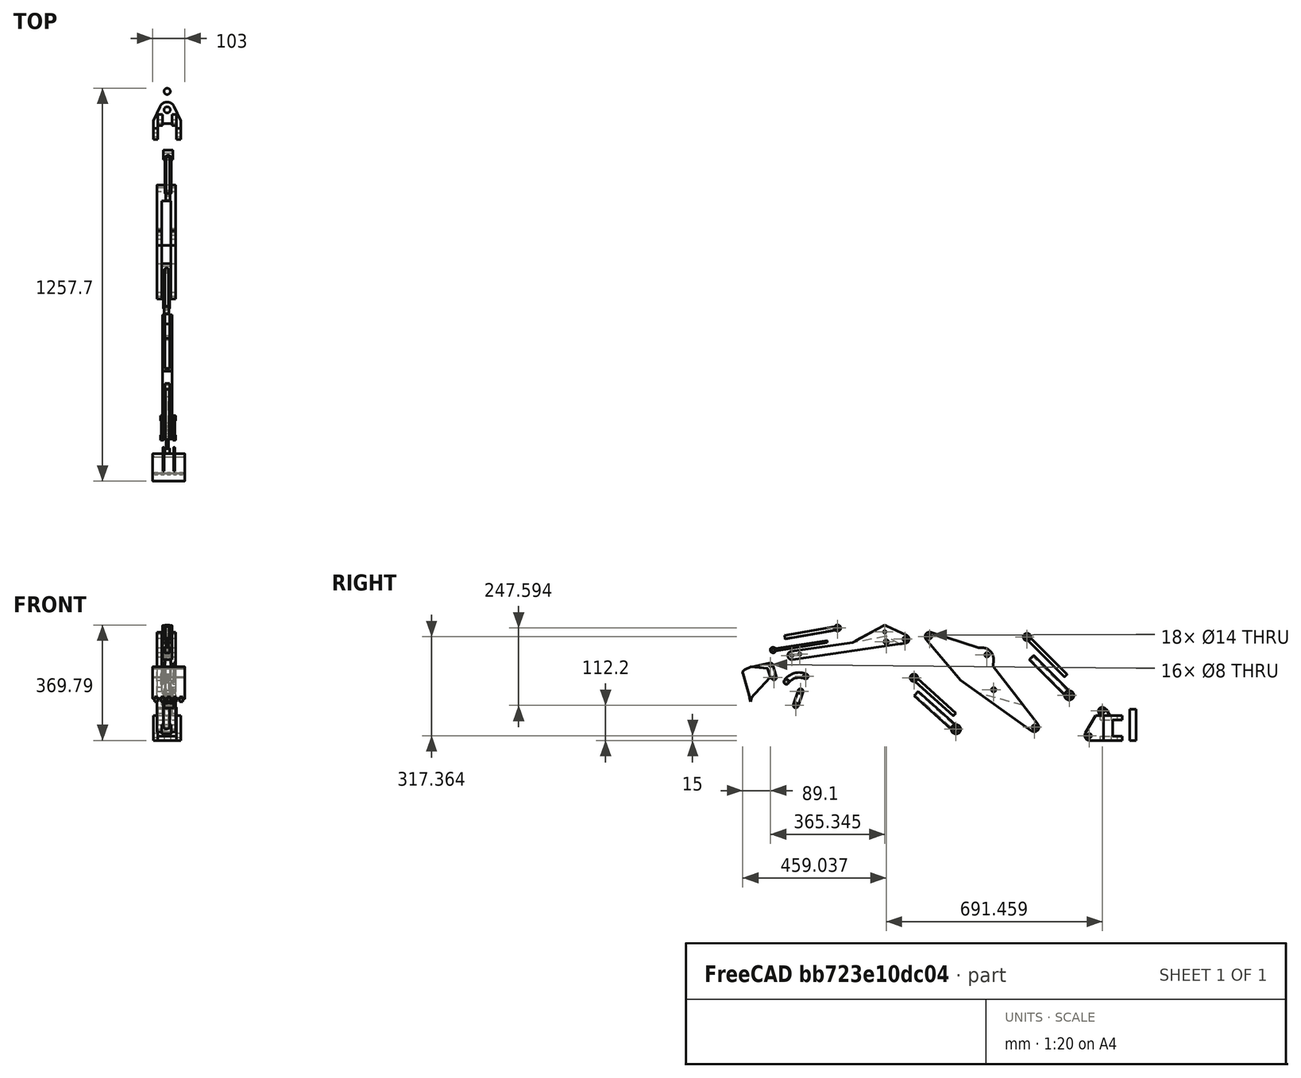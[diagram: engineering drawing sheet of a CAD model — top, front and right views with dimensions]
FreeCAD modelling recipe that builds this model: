
FCSTD DOCUMENT  (FreeCAD 0.22R38008 (Git))
Label: AssemblyExample
License: CC-BY 4.0
LicenseURL: https://creativecommons.org/licenses/by/4.0/
objects: App::FeaturePython×17, Part::Feature×13, App::Link×13, App::DocumentObjectGroup×1, Assembly::JointGroup×1, Assembly::AssemblyObject×1
note: 13 computed .brp shape members not serialized (recipe doc carries the construction recipe); baked Part::Feature solids carry a one-line shape summary decoded from their .brp

FEATURE [Part::Feature] Shape001  label="Base"
  shape: bbox 88 x 119.5 x 106 mm, 44 faces (baked)
FEATURE [Part::Feature] Shape012  label="BasePin"
  shape: bbox 20 x 20 x 100 mm, 3 faces (baked)
FEATURE [Part::Feature] Shape013  label="Stick"
  shape: bbox 30 x 388.4 x 109.8 mm, 24 faces (baked)
FEATURE [Part::Feature] Shape014  label="BucketLink1"
  shape: bbox 30 x 31.36 x 61.47 mm, 22 faces (baked)
FEATURE [Part::Feature] Shape015  label="Bucket"
  shape: bbox 103 x 108.6 x 124 mm, 97 faces (baked)
FEATURE [Part::Feature] Shape016  label="BoomCylinderInner"
  shape: bbox 15 x 140.2 x 140.2 mm, 6 faces (baked)
FEATURE [Part::Feature] Shape017  label="StickCylinderInner"
  shape: bbox 15 x 146.3 x 133.8 mm, 6 faces (baked)
FEATURE [Part::Feature] Shape018  label="BucketCylinderInner"
  shape: bbox 15 x 182.7 x 39.88 mm, 6 faces (baked)
FEATURE [Part::Feature] Shape019  label="BucketLink2"
  shape: bbox 48 x 78 x 37.57 mm, 23 faces (baked)
FEATURE [Part::Feature] Shape020  label="BoomCylinderOuter"
  shape: bbox 30 x 143 x 143 mm, 8 faces (baked)
FEATURE [Part::Feature] Shape021  label="StickCylinderOuter"
  shape: bbox 30 x 148.8 x 136.9 mm, 8 faces (baked)
FEATURE [Part::Feature] Shape022  label="BucketCylinderOuter"
  shape: bbox 15 x 179.4 x 45.6 mm, 10 faces (baked)
FEATURE [Part::Feature] Shape  label="Boom"
  shape: bbox 60 x 364 x 319 mm, 31 faces (baked)
FEATURE [App::DocumentObjectGroup] Group  label="CAD"
  Group = -> [Shape001,Shape012,Shape013,Shape014,Shape015,Shape016,Shape017,Shape018,Shape019,Shape020,Shape021,Shape022,Shape]
FEATURE [App::Link] BasePin  label="BasePin001"
  LinkPlacement = pos=(-206.517,40.2557,364.268) rot=(0,0,1;0rad)
  LinkedObject = -> Shape012
  Placement = pos=(-206.517,40.2557,364.268) rot=(0,0,1;0rad)
FEATURE [App::Link] Base  label="Base001"
  LinkPlacement = pos=(-206.517,99.4157,364.268) rot=(0,0,-1;0.004633rad)
  LinkedObject = -> Shape001
  Placement = pos=(-206.517,99.4157,364.268) rot=(0,0,-1;0.004633rad)
FEATURE [App::Link] Boom  label="Boom001"
  LinkPlacement = pos=(-202.932,230.97,229.247) rot=(-0.999947,0.002316,-0.010058;0.452746rad)
  LinkedObject = -> Shape
  Placement = pos=(-202.932,230.97,229.247) rot=(-0.999947,0.002316,-0.010058;0.452746rad)
FEATURE [App::Link] Stick  label="Stick001"
  LinkPlacement = pos=(-205.469,390.408,208.421) rot=(-0.999934,0.002316,-0.011244;0.406359rad)
  LinkedObject = -> Shape013
  Placement = pos=(-205.469,390.408,208.421) rot=(-0.999934,0.002316,-0.011244;0.406359rad)
FEATURE [App::Link] Bucket  label="Bucket001"
  LinkPlacement = pos=(-210.075,432.194,196.62) rot=(-0.99995,0.002316,-0.009747;0.466683rad)
  LinkedObject = -> Shape015
  Placement = pos=(-210.075,432.194,196.62) rot=(-0.99995,0.002316,-0.009747;0.466683rad)
FEATURE [App::Link] BucketLink2  label="BucketLink003"
  LinkPlacement = pos=(-215.535,-1246.73,276.477) rot=(0.999997,-0.002316,0.001009;3.9632rad)
  LinkedObject = -> Shape019
  Placement = pos=(-215.535,-1246.73,276.477) rot=(0.999997,-0.002316,0.001009;3.9632rad)
FEATURE [App::Link] BucketLink1  label="BucketLink004"
  LinkPlacement = pos=(-212.089,-2.4321,-20.3863) rot=(-0.999989,0.002316,-0.004149;1.01849rad)
  LinkedObject = -> Shape014
  Placement = pos=(-212.089,-2.4321,-20.3863) rot=(-0.999989,0.002316,-0.004149;1.01849rad)
FEATURE [App::Link] BoomCylinderOuter  label="BoomCylinderOuter001"
  LinkPlacement = pos=(-209.106,136.254,268.963) rot=(-0.999935,0.002316,-0.011152;0.409629rad)
  LinkedObject = -> Shape020
  Placement = pos=(-209.106,136.254,268.963) rot=(-0.999935,0.002316,-0.011152;0.409629rad)
FEATURE [App::Link] BoomCylinderInner  label="BoomCylinderInner001"
  LinkPlacement = pos=(-208.727,108.582,238.805) rot=(-0.999935,0.002316,-0.011152;0.409629rad)
  LinkedObject = -> Shape016
  Placement = pos=(-208.727,108.582,238.805) rot=(-0.999935,0.002316,-0.011152;0.409629rad)
FEATURE [App::Link] StickCylinderInner  label="StickCylinderInner001"
  LinkPlacement = pos=(-203.709,310.952,236.711) rot=(-0.999971,0.002316,-0.007276;0.616456rad)
  LinkedObject = -> Shape017
  Placement = pos=(-203.709,310.952,236.711) rot=(-0.999971,0.002316,-0.007276;0.616456rad)
FEATURE [App::Link] StickCylinderOuter  label="StickCylinderOuter001"
  LinkPlacement = pos=(-203.027,347.623,221.922) rot=(-0.999971,0.002316,-0.007276;0.616456rad)
  LinkedObject = -> Shape021
  Placement = pos=(-203.027,347.623,221.922) rot=(-0.999971,0.002316,-0.007276;0.616456rad)
FEATURE [App::Link] BucketCylinderInner  label="BucketCylinderInner001"
  LinkPlacement = pos=(-205.355,395.972,110.555) rot=(-0.999962,0.002316,-0.008436;0.535995rad)
  LinkedObject = -> Shape018
  Placement = pos=(-205.355,395.972,110.555) rot=(-0.999962,0.002316,-0.008436;0.535995rad)
FEATURE [App::Link] BucketCylinderOuter  label="BucketCylinderOuter001"
  LinkPlacement = pos=(-205.403,417.48,46.5045) rot=(-0.999964,0.002316,-0.008156;0.553448rad)
  LinkedObject = -> Shape022
  Placement = pos=(-205.403,417.48,46.5045) rot=(-0.999964,0.002316,-0.008156;0.553448rad)
FEATURE [App::FeaturePython] GroundedJoint  # Assembly grounded joint (typed FeaturePython)
  ObjectToGround = -> BasePin
  Placement = pos=(-206.517,40.2557,364.268) rot=(0,0,1;0rad)
FEATURE [App::FeaturePython] Revolute  # Assembly joint (typed FeaturePython)
  Activated = true
  AngleMax = 0
  AngleMin = 0
  Detach1 = false
  Detach2 = false
  Distance = 0
  Distance2 = 0
  EnableAngleMax = false
  EnableAngleMin = false
  EnableLengthMax = false
  EnableLengthMin = false
  JointType = 1 (Revolute)
  LengthMax = 0
  LengthMin = 0
  Object1 = -> BasePin [Face1,Edge2]
  Object2 = -> Base [Edge107,Edge107]
  Offset = (0,0,0)
  Part1 = -> BasePin
  Part2 = -> Base
  Placement1 = pos=(0,59.16,0) rot=(0,0,1;1.5708rad)
  Placement2 = pos=(0,0,0) rot=(0.707107,0.707107,0;3.14159rad)
  Rotation = 0
FEATURE [App::FeaturePython] Revolute001  # Assembly joint (typed FeaturePython)
  Activated = true
  AngleMax = 45
  AngleMin = -45
  Detach1 = false
  Detach2 = false
  Distance = 0
  Distance2 = 0
  EnableAngleMax = true
  EnableAngleMin = true
  EnableLengthMax = false
  EnableLengthMin = false
  JointType = 1 (Revolute)
  LengthMax = 0
  LengthMin = 0
  Object1 = -> Boom [Face1,Edge5]
  Object2 = -> Base [Edge61,Edge61]
  Offset = (0,0,0)
  Part1 = -> Boom
  Part2 = -> Base
  Placement1 = pos=(-32.9758,-255.877,42.3644) rot=(0.57735,0.57735,0.57735;2.0944rad)
  Placement2 = pos=(-30,-80,15) rot=(-0.57735,-0.57735,0.57735;2.0944rad)
  Rotation = 0
FEATURE [App::FeaturePython] Revolute002  # Assembly joint (typed FeaturePython)
  Activated = true
  AngleMax = 0
  AngleMin = 0
  Detach1 = false
  Detach2 = false
  Distance = 0
  Distance2 = 0
  EnableAngleMax = false
  EnableAngleMin = false
  EnableLengthMax = false
  EnableLengthMin = false
  JointType = 1 (Revolute)
  LengthMax = 0
  LengthMin = 0
  Object1 = -> BoomCylinderOuter [Edge8,Edge8]
  Object2 = -> Base [Edge34,Edge34]
  Offset = (0,0,0)
  Part1 = -> BoomCylinderOuter
  Part2 = -> Base
  Placement1 = pos=(-12.24,-144.25,144.25) rot=(0.678598,0.281085,0.678598;2.59356rad)
  Placement2 = pos=(-15,-38.0444,94.4593) rot=(0.57735,-0.57735,0.57735;4.18879rad)
  Rotation = 0
FEATURE [App::FeaturePython] Slider  # Assembly joint (typed FeaturePython)
  Activated = true
  AngleMax = 0
  AngleMin = 0
  Detach1 = false
  Detach2 = false
  Distance = 0
  Distance2 = 0
  EnableAngleMax = false
  EnableAngleMin = false
  EnableLengthMax = true
  EnableLengthMin = false
  JointType = 3 (Slider)
  LengthMax = 80
  LengthMin = 52.0086
  Object1 = -> BoomCylinderInner [Face1,Face1]
  Object2 = -> BoomCylinderOuter [Face1,Edge3]
  Offset = (0,0,0)
  Part1 = -> BoomCylinderInner
  Part2 = -> BoomCylinderOuter
  Placement1 = pos=(2.252,-213.159,265.212) rot=(0,-0.382683,0.92388;3.14159rad)
  Placement2 = pos=(2.76,-265.165,265.165) rot=(0,-0.382683,0.92388;3.14159rad)
  Rotation = 0
FEATURE [App::FeaturePython] Cylindrical  # Assembly joint (typed FeaturePython)
  Activated = true
  AngleMax = 0
  AngleMin = 0
  Detach1 = false
  Detach2 = false
  Distance = 0
  Distance2 = 0
  EnableAngleMax = false
  EnableAngleMin = false
  EnableLengthMax = false
  EnableLengthMin = false
  JointType = 2 (Cylindrical)
  LengthMax = 0
  LengthMin = 0
  Object1 = -> BoomCylinderInner [Edge7,Edge7]
  Object2 = -> Boom [Edge53,Edge53]
  Offset = (0,0,0)
  Part1 = -> BoomCylinderInner
  Part2 = -> Boom
  Placement1 = pos=(-5.248,-279.1,331.153) rot=(0.678598,-0.281085,0.678598;3.68962rad)
  Placement2 = pos=(-17.9758,-407.377,273.864) rot=(0.57735,0.57735,-0.57735;4.18879rad)
  Rotation = 0
FEATURE [App::FeaturePython] Revolute003  # Assembly joint (typed FeaturePython)
  Activated = true
  AngleMax = -23
  AngleMin = -48
  Detach1 = false
  Detach2 = false
  Distance = 0
  Distance2 = 0
  EnableAngleMax = true
  EnableAngleMin = true
  EnableLengthMax = false
  EnableLengthMin = false
  JointType = 1 (Revolute)
  LengthMax = 0
  LengthMin = 0
  Object1 = -> StickCylinderOuter [Face2,Edge3]
  Object2 = -> Boom [Edge66,Edge66]
  Offset = (0,0,0)
  Part1 = -> StickCylinderOuter
  Part2 = -> Boom
  Placement1 = pos=(12.66,-506.596,35.8372) rot=(0.682415,0.261954,0.682415;2.6292rad)
  Placement2 = pos=(12.0242,-385.877,162.364) rot=(0.57735,0.57735,-0.57735;4.18879rad)
  Rotation = 0
FEATURE [App::FeaturePython] Slider001  # Assembly joint (typed FeaturePython)
  Activated = true
  AngleMax = 0
  AngleMin = 0
  Detach1 = false
  Detach2 = false
  Distance = 0
  Distance2 = 0
  EnableAngleMax = false
  EnableAngleMin = false
  EnableLengthMax = true
  EnableLengthMin = false
  JointType = 3 (Slider)
  LengthMax = 80
  LengthMin = 63.2772
  Object1 = -> StickCylinderInner [Face1,Face1]
  Object2 = -> StickCylinderOuter [Face6,Edge3]
  Offset = (0,0,0)
  Part1 = -> StickCylinderInner
  Part2 = -> StickCylinderOuter
  Placement1 = pos=(-1.828,-571.574,138.121) rot=(0,-0.406737,0.913545;3.14159rad)
  Placement2 = pos=(-2.34,-633.674,150.259) rot=(0,-0.406737,0.913545;3.14159rad)
  Rotation = 0
FEATURE [App::FeaturePython] Revolute004  # Assembly joint (typed FeaturePython)
  Activated = true
  AngleMax = 0
  AngleMin = 0
  Detach1 = false
  Detach2 = false
  Distance = 0
  Distance2 = 0
  EnableAngleMax = false
  EnableAngleMin = false
  EnableLengthMax = false
  EnableLengthMin = false
  JointType = 1 (Revolute)
  LengthMax = 0
  LengthMin = 0
  Object1 = -> Stick [Edge41,Edge41]
  Object2 = -> Boom [Edge51,Edge51]
  Offset = (0,0,0)
  Part1 = -> Stick
  Part2 = -> Boom
  Placement1 = pos=(-14.7,-729.503,315.527) rot=(0.363936,0.85738,0.363936;1.72407rad)
  Placement2 = pos=(-17.9758,-590.877,332.364) rot=(0.57735,0.57735,-0.57735;4.18879rad)
  Rotation = 0
FEATURE [App::FeaturePython] Cylindrical001  # Assembly joint (typed FeaturePython)
  Activated = true
  AngleMax = 0
  AngleMin = 0
  Detach1 = false
  Detach2 = false
  Distance = 0
  Distance2 = 0
  EnableAngleMax = false
  EnableAngleMin = false
  EnableLengthMax = false
  EnableLengthMin = false
  JointType = 2 (Cylindrical)
  LengthMax = 0
  LengthMin = 0
  Object1 = -> Stick [Edge57,Edge57]
  Object2 = -> StickCylinderInner [Face4,Face4]
  Offset = (0,0,0)
  Part1 = -> Stick
  Part2 = -> StickCylinderInner
  Placement1 = pos=(-7.2,-669.12,324.36) rot=(0.363936,0.85738,0.363936;1.72407rad)
  Placement2 = pos=(-9.328,-640.876,200.52) rot=(0.674471,-0.300294,0.674471;3.72505rad)
  Rotation = 0
FEATURE [App::FeaturePython] Revolute005  # Assembly joint (typed FeaturePython)
  Activated = true
  AngleMax = -120
  AngleMin = -145
  Detach1 = false
  Detach2 = false
  Distance = 0
  Distance2 = 0
  EnableAngleMax = true
  EnableAngleMin = true
  EnableLengthMax = false
  EnableLengthMin = false
  JointType = 1 (Revolute)
  LengthMax = 0
  LengthMin = 0
  Object1 = -> BucketCylinderOuter [Face6,Face6]
  Object2 = -> Stick [Edge56,Edge56]
  Offset = (0,0,0)
  Part1 = -> BucketCylinderOuter
  Part2 = -> Stick
  Placement1 = pos=(-7.14,-885.253,359.794) rot=(0.705758,-0.061746,0.705758;3.26493rad)
  Placement2 = pos=(-7.2,-734.095,347.625) rot=(0.363936,0.85738,0.363936;1.72407rad)
  Rotation = 0
FEATURE [App::FeaturePython] Slider002  # Assembly joint (typed FeaturePython)
  Activated = true
  AngleMax = 0
  AngleMin = 0
  Detach1 = false
  Detach2 = false
  Distance = 0
  Distance2 = 0
  EnableAngleMax = false
  EnableAngleMin = false
  EnableLengthMax = true
  EnableLengthMin = false
  JointType = 3 (Slider)
  LengthMax = 0
  LengthMin = 0
  Object1 = -> BucketCylinderInner [Face1,Face1]
  Object2 = -> BucketCylinderOuter [Face1,Face1]
  Offset = (0,0,0)
  Part1 = -> BucketCylinderInner
  Part2 = -> BucketCylinderOuter
  Placement1 = pos=(0.212,-1000.72,303.69) rot=(0,-0.760406,0.649448;3.14159rad)
  Placement2 = pos=(0.36,-974.049,344.137) rot=(0,-0.766044,0.642788;3.14159rad)
  Rotation = 0
FEATURE [App::FeaturePython] Revolute006  # Assembly joint (typed FeaturePython)
  Activated = true
  AngleMax = 0
  AngleMin = 0
  Detach1 = false
  Detach2 = false
  Distance = 0
  Distance2 = 0
  EnableAngleMax = false
  EnableAngleMin = false
  EnableLengthMax = false
  EnableLengthMin = false
  JointType = 1 (Revolute)
  LengthMax = 0
  LengthMin = 0
  Object1 = -> BucketLink2 [Edge49,Edge49]
  Object2 = -> Stick [Face20,Edge10]
  Offset = (0,0,0)
  Part1 = -> BucketLink2
  Part2 = -> Stick
  Placement1 = pos=(-12.2189,-987.052,204.816) rot=(-0.707107,0,-0.707107;3.14159rad)
  Placement2 = pos=(-14.7,-1006.04,276.188) rot=(0.363936,0.85738,0.363936;1.72407rad)
  Rotation = 0
FEATURE [App::FeaturePython] Revolute007  # Assembly joint (typed FeaturePython)
  Activated = true
  AngleMax = 0
  AngleMin = 0
  Detach1 = false
  Detach2 = false
  Distance = 0
  Distance2 = 0
  EnableAngleMax = false
  EnableAngleMin = false
  EnableLengthMax = false
  EnableLengthMin = false
  JointType = 1 (Revolute)
  LengthMax = 0
  LengthMin = 0
  Object1 = -> Bucket [Edge139,Edge139]
  Object2 = -> Stick [Face20,Edge6]
  Offset = (0,0,0)
  Part1 = -> Bucket
  Part2 = -> Stick
  Placement1 = pos=(-9.9,-1088.34,200.94) rot=(0.57735,0.57735,0.57735;2.0944rad)
  Placement2 = pos=(-14.7,-1031.22,271.858) rot=(0.363936,0.85738,0.363936;1.72407rad)
  Rotation = 0
FEATURE [App::FeaturePython] Revolute008  # Assembly joint (typed FeaturePython)
  Activated = true
  AngleMax = 0
  AngleMin = 0
  Detach1 = false
  Detach2 = false
  Distance = 0
  Distance2 = 0
  EnableAngleMax = false
  EnableAngleMin = false
  EnableLengthMax = false
  EnableLengthMin = false
  JointType = 1 (Revolute)
  LengthMax = 0
  LengthMin = 0
  Object1 = -> BucketLink1 [Face11,Face11]
  Object2 = -> Bucket [Face65,Edge2]
  Offset = (0,0,0)
  Part1 = -> BucketLink1
  Part2 = -> Bucket
  Placement1 = pos=(-9.9,-1018.98,112.2) rot=(0.57735,0.57735,0.57735;2.0944rad)
  Placement2 = pos=(-9.9,-1099.44,240.39) rot=(0.57735,0.57735,0.57735;2.0944rad)
  Rotation = 0
FEATURE [App::FeaturePython] Cylindrical002  # Assembly joint (typed FeaturePython)
  Activated = true
  AngleMax = 0
  AngleMin = 0
  Detach1 = false
  Detach2 = false
  Distance = 0
  Distance2 = 0
  EnableAngleMax = false
  EnableAngleMin = false
  EnableLengthMax = false
  EnableLengthMin = false
  JointType = 2 (Cylindrical)
  LengthMax = 0
  LengthMin = 0
  Object1 = -> BucketLink1 [Edge25,Edge25]
  Object2 = -> BucketLink2 [Face13,Face13]
  Offset = (0,0,0)
  Part1 = -> BucketLink1
  Part2 = -> BucketLink2
  Placement1 = pos=(-2.9,-1003.62,157.675) rot=(0.57735,0.57735,0.57735;2.0944rad)
  Placement2 = pos=(2.78108,-1049.05,187.816) rot=(-0.57735,-0.57735,-0.57735;4.18879rad)
  Rotation = 0
FEATURE [App::FeaturePython] Cylindrical003  # Assembly joint (typed FeaturePython)
  Activated = true
  AngleMax = 0
  AngleMin = 0
  Detach1 = false
  Detach2 = false
  Distance = 0
  Distance2 = 0
  EnableAngleMax = false
  EnableAngleMin = false
  EnableLengthMax = false
  EnableLengthMin = false
  JointType = 2 (Cylindrical)
  LengthMax = 0
  LengthMin = 0
  Object1 = -> BucketCylinderInner [Face3,Face3]
  Object2 = -> BucketLink2 [Face13,Face13]
  Offset = (0,0,0)
  Part1 = -> BucketCylinderInner
  Part2 = -> BucketLink2
  Placement1 = pos=(0.211998,-1091.57,289.302) rot=(0.544663,-0.637718,0.544663;4.27698rad)
  Placement2 = pos=(2.78108,-1049.05,187.816) rot=(-0.57735,-0.57735,-0.57735;4.18879rad)
  Rotation = 0
FEATURE [Assembly::JointGroup] Joints
  Group = -> [GroundedJoint,Revolute,Revolute001,Revolute002,Slider,Cylindrical,Revolute003,Slider001,Revolute004,Cylindrical001,Revolute005,Slider002,Revolute006,Revolute007,Revolute008,Cylindrical002,Cylindrical003]
FEATURE [Assembly::AssemblyObject] Assembly
  Group = -> [Joints,BasePin,Base,Boom,Stick,Bucket,BucketLink2,BucketLink1,BoomCylinderOuter,BoomCylinderInner,StickCylinderInner,StickCylinderOuter,BucketCylinderInner,BucketCylinderOuter,GroundedJoint,Revolute,Revolute001,Revolute002,Slider,Cylindrical,Revolute003,Slider001,Revolute004,Cylindrical001,Revolute005,Slider002,Revolute006,Revolute007,Revolute008,Cylindrical002,Cylindrical003]
  Origin = -> Origin
  Type = Assembly
